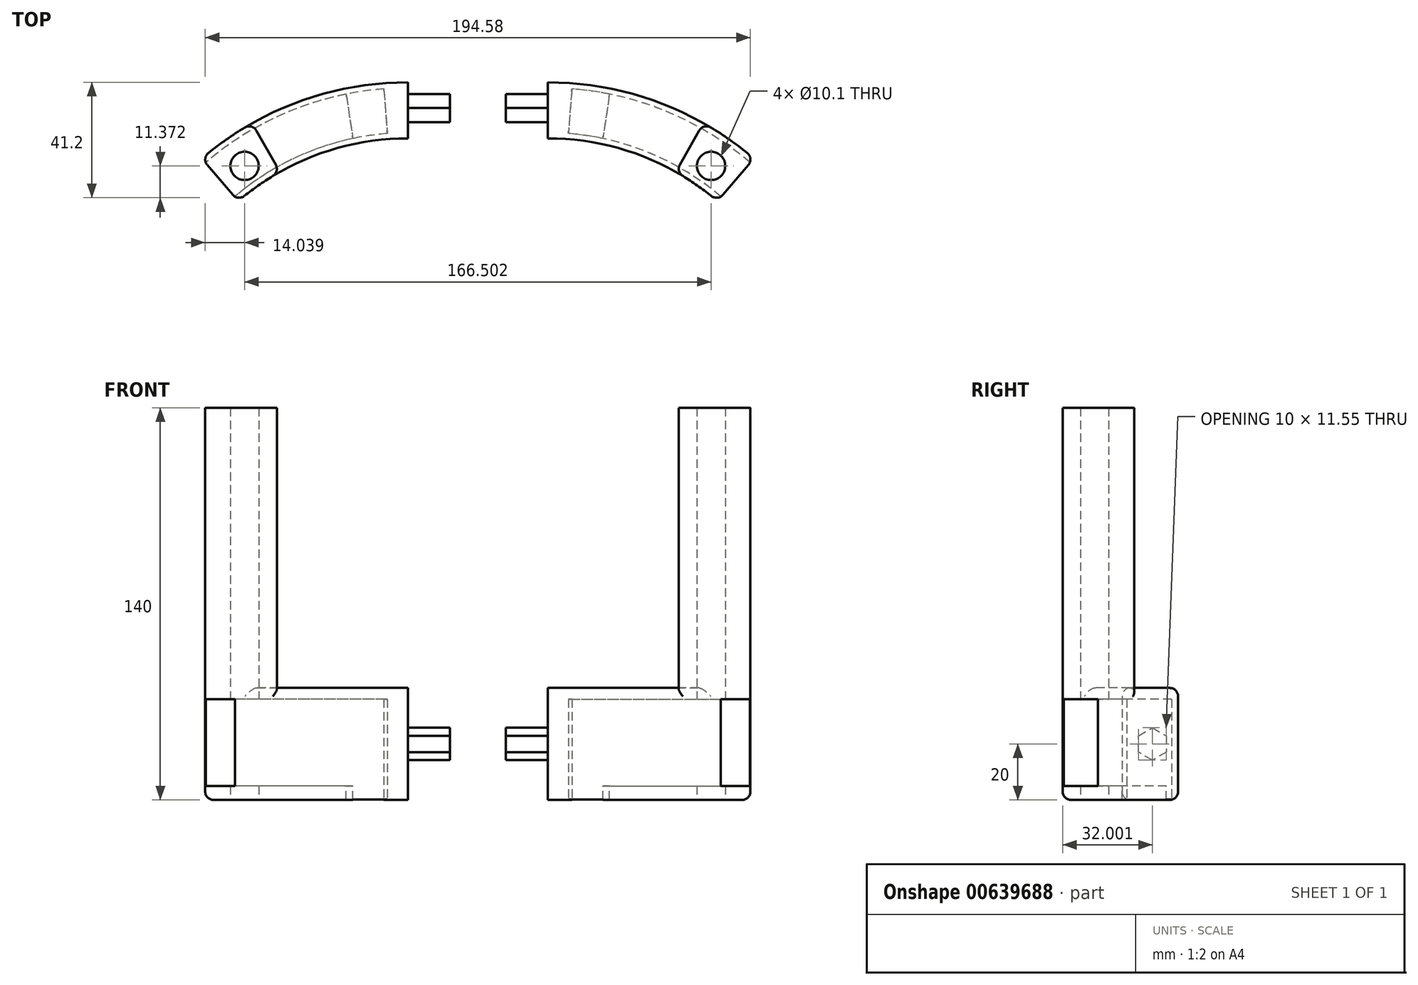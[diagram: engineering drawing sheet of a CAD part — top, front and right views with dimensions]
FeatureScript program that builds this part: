
annotation { "Feature Type Name" : "Feature", "Feature Type Description" : "" }
export const myFeature = defineFeature(function(context is Context, id is Id, definition is map)
    precondition{}
    {
        {
            var Q0;
            Q0=qCreatedBy(makeId("Top.planeOp"),FACE);
            var sketch = newSketch(context, id + "F0", { "sketchPlane" : qUnion([Q0])});
            skArc(sketch, "E0", {"start": v(0, 113) * mm, "mid": v(-39.2, 105.98) * mm, "end": v(-73.54, 85.8) * mm});
            skArc(sketch, "E1", {"start": v(0, 93) * mm, "mid": v(-32.27, 87.22) * mm, "end": v(-60.53, 70.6) * mm});
            skLineSegment(sketch, "E2", {"start": v(0, 113) * mm, "end": v(0, 93) * mm});
            skLineSegment(sketch, "E3", {"start": v(-73.54, 85.8) * mm, "end": v(-60.53, 70.6) * mm});
            skLineSegment(sketch, "E4", {"start": v(-55.48, 98.44) * mm, "end": v(-45.66, 81.02) * mm});
            skCircle(sketch, "E5", {"center": v(-58.25, 83.17) * mm, "radius": 5.05 * mm});
            skSolve(sketch);
        }
        {
            var Q0;
            {var subQ0=sQuery(id+"F0.wireOp",EDGE,"E2");Q0=makeQuery(id+"F0.imprint","IMPRINT",FACE,{"disambiguationData":[TD([[makeQuery(id+"F0.imprint","IMPRINT",EDGE,{"derivedFrom":subQ0}),-1.0]])]});}
            extrude(context, id + "F1", {"entities" : qUnion([Q0]), "depth" : 40 * mm, "offsetDistance" : 25 * mm});
        }
        {
            var Q0;
            {var subQ0=sQuery(id+"F0.wireOp",EDGE,"E3");Q0=makeQuery(id+"F0.imprint","IMPRINT",FACE,{"disambiguationData":[TD([[makeQuery(id+"F0.imprint","IMPRINT",EDGE,{"derivedFrom":subQ0}),1.0]])]});}
            extrude(context, id + "F2", {"entities" : qUnion([Q0]), "operationType" : NewBodyOperationType.ADD, "depth" : 140 * mm, "offsetDistance" : 25 * mm});
        }
        {
            var Q0;
            Q0=qCreatedBy(makeId("Right.planeOp"),FACE);
            var sketch = newSketch(context, id + "F3", { "sketchPlane" : qUnion([Q0])});
            skCircle(sketch, "E6.cCircle", {"center": v(103.8, 20) * mm, "radius": 5 * mm, "construction": true});
            skLineSegment(sketch, "E6.0", {"start": v(108.8, 22.89) * mm, "end": v(108.8, 17.11) * mm});
            skLineSegment(sketch, "E6.1", {"start": v(108.8, 17.11) * mm, "end": v(103.8, 14.23) * mm});
            skLineSegment(sketch, "E6.2", {"start": v(103.8, 14.23) * mm, "end": v(98.8, 17.11) * mm});
            skLineSegment(sketch, "E6.3", {"start": v(98.8, 17.11) * mm, "end": v(98.8, 22.89) * mm});
            skLineSegment(sketch, "E6.4", {"start": v(98.8, 22.89) * mm, "end": v(103.8, 25.77) * mm});
            skLineSegment(sketch, "E6.5", {"start": v(103.8, 25.77) * mm, "end": v(108.8, 22.89) * mm});
            skPoint(sketch, "E6.0.midPoint", {"position": v(108.8, 20) * mm});
            skSolve(sketch);
        }
        {
            var Q0;
            Q0 = qSketchRegion(id + "F3", true);
            extrude(context, id + "F4", {"entities" : qUnion([Q0]), "operationType" : NewBodyOperationType.ADD, "depth" : 15 * mm, "offsetDistance" : 25 * mm});
        }
        {
            var Q0;
            Q0=qCreatedBy(makeId("Top.planeOp"),FACE);
            cPlane(context, id + "F5", {"entities" : qUnion([Q0]), "cplaneType" : CPlaneType.OFFSET, "offset" : 5 * mm, "width" : 150 * mm, "height" : 150 * mm});
        }
        {
            var Q0;
            Q0=qCreatedBy(id+"F5.planeOp",FACE);
            var sketch = newSketch(context, id + "F6", { "sketchPlane" : qUnion([Q0])});
            skArc(sketch, "E7", {"start": v(-8.55, 110.67) * mm, "mid": v(-48.75, 99.72) * mm, "end": v(-82.08, 74.72) * mm});
            skArc(sketch, "E8", {"start": v(-7.32, 94.72) * mm, "mid": v(-41.73, 85.35) * mm, "end": v(-70.25, 63.95) * mm});
            skLineSegment(sketch, "E9", {"start": v(-8.55, 110.67) * mm, "end": v(-7.32, 94.72) * mm});
            skLineSegment(sketch, "E10", {"start": v(-82.08, 74.72) * mm, "end": v(-70.25, 63.95) * mm});
            skLineSegment(sketch, "E11", {"start": v(-22, 108.8) * mm, "end": v(-19.6, 92.95) * mm});
            skSolve(sketch);
        }
        {
            var Q0;
            Q0 = qSketchRegion(id + "F6", true);
            extrude(context, id + "F7", {"entities" : qUnion([Q0]), "operationType" : NewBodyOperationType.REMOVE, "depth" : 31 * mm, "offsetDistance" : 25 * mm});
        }
        {
            var Q0;
            {var subQ0=sQuery(id+"F6.wireOp",EDGE,"E9");Q0=makeQuery(id+"F6.imprint","IMPRINT",FACE,{"disambiguationData":[TD([[makeQuery(id+"F6.imprint","IMPRINT",EDGE,{"derivedFrom":subQ0}),-1.0]])]});}
            extrude(context, id + "F8", {"entities" : qUnion([Q0]), "operationType" : NewBodyOperationType.REMOVE, "oppositeDirection" : true, "depth" : 25 * mm, "offsetDistance" : 25 * mm});
        }
        {
            var Q0;
            {var subQ0=sQuery(id+"F0.wireOp",EDGE,"E0");Q0=makeQuery(id+"F2.boolean.opBoolean","MERGE",EDGE,{"derivedFrom":[makeQuery(id+"F1.opExtrude","CAP_EDGE",EDGE,{"disambiguationData":[OSD([subQ0])],"isStart":true}),makeQuery(id+"F2.opExtrude","CAP_EDGE",EDGE,{"disambiguationData":[OSD([subQ0])],"isStart":true})]});}
            var Q1;
            Q1=makeQuery(id+"F2.opExtrude","CAP_EDGE",EDGE,{"disambiguationData":[OSD([sQuery(id+"F0.wireOp",EDGE,"E3")])],"isStart":true});
            var Q2;
            {var subQ0=sQuery(id+"F0.wireOp",EDGE,"E1");Q2=makeQuery(id+"F2.boolean.opBoolean","MERGE",EDGE,{"derivedFrom":[makeQuery(id+"F1.opExtrude","CAP_EDGE",EDGE,{"disambiguationData":[OSD([subQ0])],"isStart":true}),makeQuery(id+"F2.opExtrude","CAP_EDGE",EDGE,{"disambiguationData":[OSD([subQ0])],"isStart":true})]});}
            var Q3;
            Q3=makeQuery(id+"F1.opExtrude","CAP_EDGE",EDGE,{"disambiguationData":[OSD([sQuery(id+"F0.wireOp",EDGE,"E0")])],"isStart":false});
            var Q4;
            Q4=makeQuery(id+"F1.opExtrude","CAP_EDGE",EDGE,{"disambiguationData":[OSD([sQuery(id+"F0.wireOp",EDGE,"E1")])],"isStart":false});
            var Q5;
            Q5=makeQuery(id+"F2.opExtrude","SWEPT_EDGE",EDGE,{"disambiguationData":[OSD([sQuery(id+"F0.wireOp",EDGE,"E0"),sQuery(id+"F0.wireOp",EDGE,"E4")])]});
            var Q6;
            Q6=makeQuery(id+"F2.opExtrude","SWEPT_EDGE",EDGE,{"disambiguationData":[OSD([sQuery(id+"F0.wireOp",EDGE,"E0"),sQuery(id+"F0.wireOp",EDGE,"E3")])]});
            var Q7;
            Q7=makeQuery(id+"F2.opExtrude","SWEPT_EDGE",EDGE,{"disambiguationData":[OSD([sQuery(id+"F0.wireOp",EDGE,"E1"),sQuery(id+"F0.wireOp",EDGE,"E3")])]});
            var Q8;
            Q8=makeQuery(id+"F2.opExtrude","SWEPT_EDGE",EDGE,{"disambiguationData":[OSD([sQuery(id+"F0.wireOp",EDGE,"E1"),sQuery(id+"F0.wireOp",EDGE,"E4")])]});
            fillet(context, id + "F9", {"entities" : qUnion([Q0, Q1, Q2, Q3, Q4, Q5, Q6, Q7, Q8]), "radius" : 3 * mm, "tangentPropagation" : true, "allowEdgeOverflow" : false});
        }
        {
            var Q0;
            Q0=qCreatedBy(makeId("Right.planeOp"),FACE);
            cPlane(context, id + "F10", {"entities" : qUnion([Q0]), "cplaneType" : CPlaneType.OFFSET, "offset" : 25 * mm, "width" : 150 * mm, "height" : 150 * mm});
        }
        {
            var Q0;
            Q0=makeQuery(id+"F1.opExtrude","SWEPT_BODY",BODY,{"disambiguationData":[OSD([sQuery(id+"F0.wireOp",EDGE,"E0"),sQuery(id+"F0.wireOp",EDGE,"E1"),sQuery(id+"F0.wireOp",EDGE,"E2"),sQuery(id+"F0.wireOp",EDGE,"E4")])]});
            var Q1;
            Q1=qCreatedBy(id+"F10.planeOp",FACE);
            mirror(context, id + "F11", {"entities" : qUnion([Q0]), "mirrorPlane" : qUnion([Q1])});
        }
    });
